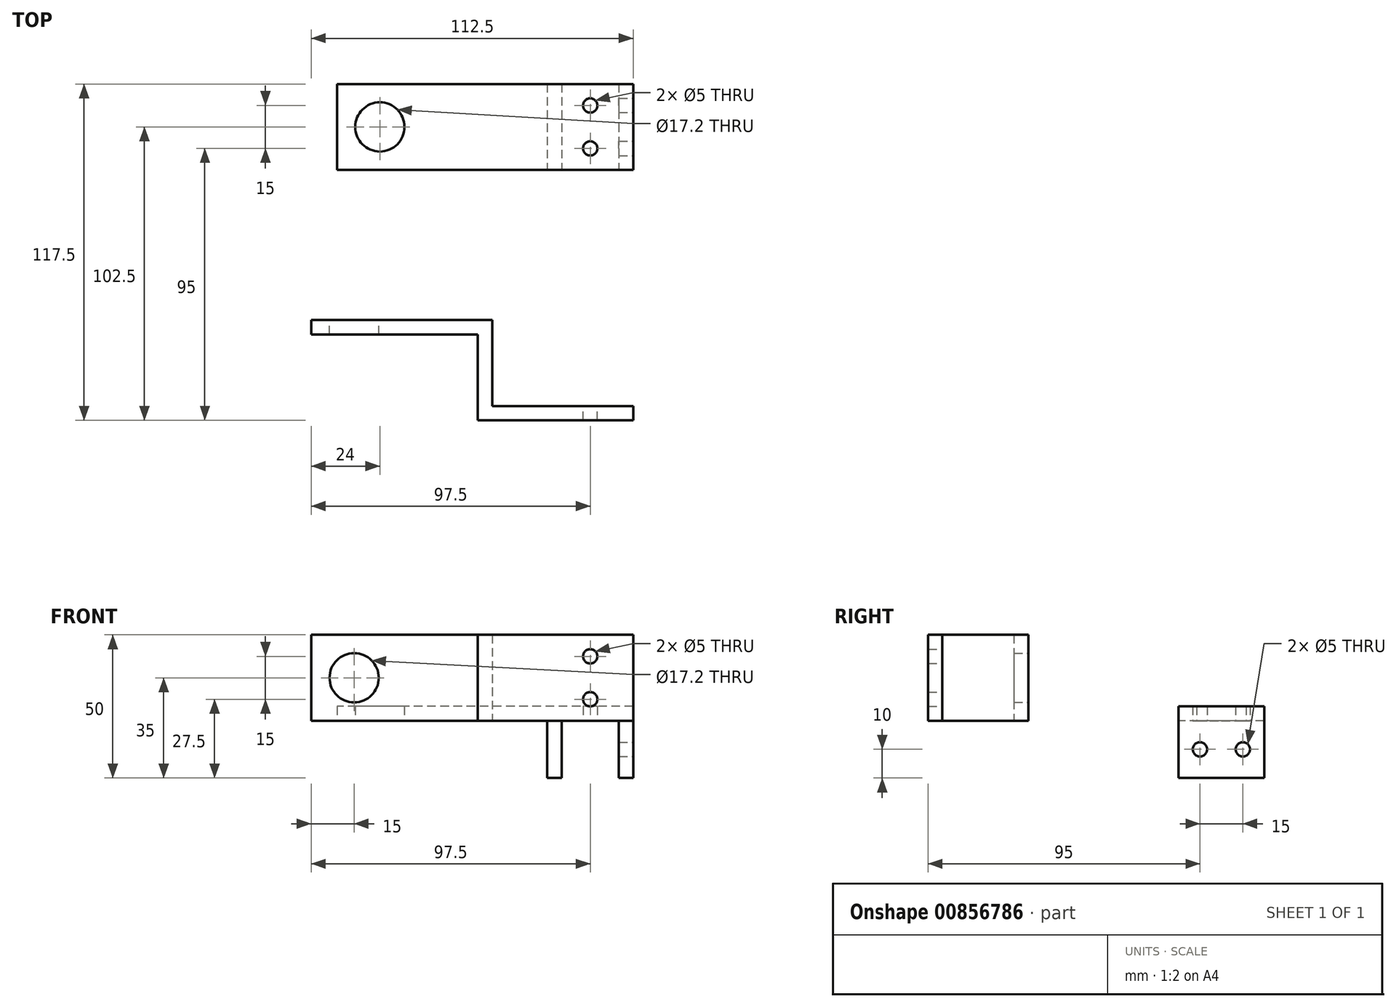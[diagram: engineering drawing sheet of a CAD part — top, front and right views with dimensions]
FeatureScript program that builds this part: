
annotation { "Feature Type Name" : "Feature", "Feature Type Description" : "" }
export const myFeature = defineFeature(function(context is Context, id is Id, definition is map)
    precondition{}
    {
        {
            var Q0;
            Q0=qCreatedBy(makeId("Top.planeOp"),FACE);
            var sketch = newSketch(context, id + "F0", { "sketchPlane" : qUnion([Q0])});
            skLineSegment(sketch, "E0.bottom", {"start": v(51.75, -15) * mm, "end": v(-51.75, -15) * mm});
            skLineSegment(sketch, "E0.top", {"start": v(51.75, 15) * mm, "end": v(-51.75, 15) * mm});
            skLineSegment(sketch, "E0.left", {"start": v(51.75, -15) * mm, "end": v(51.75, 15) * mm});
            skLineSegment(sketch, "E0.right", {"start": v(-51.75, -15) * mm, "end": v(-51.75, 15) * mm});
            skPoint(sketch, "E0.middle", {"position": v(0, 0) * mm});
            skLineSegment(sketch, "E1", {"start": v(46.75, 15) * mm, "end": v(46.75, -15) * mm});
            skCircle(sketch, "E2", {"center": v(-36.75, 0) * mm, "radius": 8.6 * mm});
            skLineSegment(sketch, "E3", {"start": v(26.75, 15) * mm, "end": v(26.75, -15) * mm});
            skLineSegment(sketch, "E4", {"start": v(21.75, 15) * mm, "end": v(21.75, -15) * mm});
            skCircle(sketch, "E5", {"center": v(36.75, 7.5) * mm, "radius": 2.5 * mm});
            skCircle(sketch, "E6", {"center": v(36.75, -7.5) * mm, "radius": 2.5 * mm});
            skLineSegment(sketch, "E7.bottom", {"start": v(51.75, -97.5) * mm, "end": v(-51.75, -97.5) * mm});
            skLineSegment(sketch, "E7.top", {"start": v(51.75, -102.5) * mm, "end": v(-51.75, -102.5) * mm});
            skLineSegment(sketch, "E7.left", {"start": v(51.75, -97.5) * mm, "end": v(51.75, -102.5) * mm});
            skLineSegment(sketch, "E7.right", {"start": v(-51.75, -97.5) * mm, "end": v(-51.75, -102.5) * mm});
            skPoint(sketch, "E7.middle", {"position": v(0, -100) * mm});
            skPoint(sketch, "E7.middle.positionSnap0", {"position": v(0, -15) * mm});
            skPoint(sketch, "E7.centerSnap0", {"position": v(0, -15) * mm});
            skLineSegment(sketch, "E8.bottom", {"start": v(51.75, -102.5) * mm, "end": v(46.75, -102.5) * mm});
            skLineSegment(sketch, "E8.top", {"start": v(51.75, -127.5) * mm, "end": v(46.75, -127.5) * mm});
            skLineSegment(sketch, "E8.left", {"start": v(51.75, -102.5) * mm, "end": v(51.75, -127.5) * mm});
            skLineSegment(sketch, "E8.right", {"start": v(46.75, -102.5) * mm, "end": v(46.75, -127.5) * mm});
            skLineSegment(sketch, "E9.bottom", {"start": v(21.75, -102.5) * mm, "end": v(26.75, -102.5) * mm});
            skLineSegment(sketch, "E9.top", {"start": v(21.75, -127.5) * mm, "end": v(26.75, -127.5) * mm});
            skLineSegment(sketch, "E9.left", {"start": v(21.75, -102.5) * mm, "end": v(21.75, -127.5) * mm});
            skLineSegment(sketch, "E9.right", {"start": v(26.75, -102.5) * mm, "end": v(26.75, -127.5) * mm});
            skLineSegment(sketch, "E10", {"start": v(2.5, -97.5) * mm, "end": v(2.5, -67.5) * mm});
            skLineSegment(sketch, "E11", {"start": v(2.5, -67.5) * mm, "end": v(-51.75, -67.5) * mm});
            skLineSegment(sketch, "E12", {"start": v(-51.75, -67.5) * mm, "end": v(-51.75, -72.5) * mm});
            skLineSegment(sketch, "E13", {"start": v(-51.75, -72.5) * mm, "end": v(-2.5, -72.5) * mm});
            skLineSegment(sketch, "E14", {"start": v(-2.5, -72.5) * mm, "end": v(-2.5, -97.5) * mm});
            skLineSegment(sketch, "E15", {"start": v(-2.5, -97.5) * mm, "end": v(-2.5, -102.5) * mm});
            skLineSegment(sketch, "E16", {"start": v(-51.75, -67.5) * mm, "end": v(-60.75, -67.5) * mm});
            skLineSegment(sketch, "E17", {"start": v(-60.75, -67.5) * mm, "end": v(-60.75, -72.5) * mm});
            skLineSegment(sketch, "E18", {"start": v(-60.75, -72.5) * mm, "end": v(-51.75, -72.5) * mm});
            skSolve(sketch);
        }
        {
            var Q0;
            {var subQ0=sQuery(id+"F0.wireOp",EDGE,"E0.left");Q0=makeQuery(id+"F0.imprint","IMPRINT",FACE,{"disambiguationData":[TD([[makeQuery(id+"F0.imprint","IMPRINT",EDGE,{"derivedFrom":subQ0}),1.0]])]});}
            var Q1;
            {var subQ0=sQuery(id+"F0.wireOp",EDGE,"E10");Q1=makeQuery(id+"F0.imprint","IMPRINT",FACE,{"disambiguationData":[TD([[makeQuery(id+"F0.imprint","IMPRINT",EDGE,{"derivedFrom":subQ0}),1.0]])]});}
            var Q2;
            Q2=makeQuery(id+"F0.imprint","IMPRINT",FACE,{"disambiguationData":[TD([[makeQuery(id+"F0.imprint","IMPRINT",EDGE,{"derivedFrom":sQuery(id+"F0.wireOp",EDGE,"E8.bottom")}),1.0]])]});
            var Q3;
            Q3=makeQuery(id+"F0.imprint","IMPRINT",FACE,{"disambiguationData":[TD([[makeQuery(id+"F0.imprint","IMPRINT",EDGE,{"derivedFrom":sQuery(id+"F0.wireOp",EDGE,"E9.bottom")}),-1.0]])]});
            var Q4;
            {var subQ0=sQuery(id+"F0.wireOp",EDGE,"E3");Q4=makeQuery(id+"F0.imprint","IMPRINT",FACE,{"disambiguationData":[TD([[makeQuery(id+"F0.imprint","IMPRINT",EDGE,{"derivedFrom":subQ0}),-1.0]])]});}
            var Q5;
            {var subQ0=sQuery(id+"F0.wireOp",EDGE,"E0.right");Q5=makeQuery(id+"F0.imprint","IMPRINT",FACE,{"disambiguationData":[TD([[makeQuery(id+"F0.imprint","IMPRINT",EDGE,{"derivedFrom":subQ0}),-1.0]])]});}
            var Q6;
            {var subQ1=sQuery(id+"F0.wireOp",EDGE,"E1");Q6=makeQuery(id+"F0.imprint","IMPRINT",FACE,{"disambiguationData":[TD([[makeQuery(id+"F0.imprint","IMPRINT",EDGE,{"derivedFrom":subQ1}),-1.0]])]});}
            var Q7;
            {var subQ6=sQuery(id+"F0.wireOp",EDGE,"E7.left");Q7=makeQuery(id+"F0.imprint","IMPRINT",FACE,{"disambiguationData":[TD([[makeQuery(id+"F0.imprint","IMPRINT",EDGE,{"derivedFrom":subQ6}),-1.0]])]});}
            extrude(context, id + "F1", {"entities" : qUnion([Q0, Q1, Q2, Q3, Q4, Q5, Q6, Q7]), "depth" : 5 * mm, "offsetDistance" : 25 * mm});
        }
        {
            var Q0;
            {var subQ0=sQuery(id+"F0.wireOp",EDGE,"E3");Q0=makeQuery(id+"F0.imprint","IMPRINT",FACE,{"disambiguationData":[TD([[makeQuery(id+"F0.imprint","IMPRINT",EDGE,{"derivedFrom":subQ0}),-1.0]])]});}
            var Q1;
            {var subQ0=sQuery(id+"F0.wireOp",EDGE,"E0.left");Q1=makeQuery(id+"F0.imprint","IMPRINT",FACE,{"disambiguationData":[TD([[makeQuery(id+"F0.imprint","IMPRINT",EDGE,{"derivedFrom":subQ0}),1.0]])]});}
            extrude(context, id + "F2", {"entities" : qUnion([Q0, Q1]), "operationType" : NewBodyOperationType.ADD, "oppositeDirection" : true, "depth" : 20 * mm, "offsetDistance" : 25 * mm});
        }
        {
            var Q0;
            {var subQ0=sQuery(id+"F0.wireOp",EDGE,"E0.left");Q0=makeQuery(id+"F2.boolean.opBoolean","MERGE",FACE,{"derivedFrom":[makeQuery(id+"F1.opExtrude","SWEPT_FACE",FACE,{"disambiguationData":[OSD([subQ0])]}),makeQuery(id+"F2.opExtrude","SWEPT_FACE",FACE,{"disambiguationData":[OSD([subQ0])]})]});}
            var sketch = newSketch(context, id + "F3", { "sketchPlane" : qUnion([Q0])});
            skCircle(sketch, "E19", {"center": v(-7.5, -10) * mm, "radius": 2.5 * mm});
            skCircle(sketch, "E20.MirrorC", {"center": v(7.5, -10) * mm, "radius": 2.5 * mm});
            skSolve(sketch);
        }
        {
            var Q0;
            Q0 = qSketchRegion(id + "F3", true);
            extrude(context, id + "F4", {"entities" : qUnion([Q0]), "operationType" : NewBodyOperationType.REMOVE, "oppositeDirection" : true, "depth" : 10 * mm, "offsetDistance" : 25 * mm});
        }
        {
            var Q0;
            {var subQ0=sQuery(id+"F0.wireOp",EDGE,"E10");Q0=makeQuery(id+"F0.imprint","IMPRINT",FACE,{"disambiguationData":[TD([[makeQuery(id+"F0.imprint","IMPRINT",EDGE,{"derivedFrom":subQ0}),1.0]])]});}
            var Q1;
            {var subQ6=sQuery(id+"F0.wireOp",EDGE,"E7.left");Q1=makeQuery(id+"F0.imprint","IMPRINT",FACE,{"disambiguationData":[TD([[makeQuery(id+"F0.imprint","IMPRINT",EDGE,{"derivedFrom":subQ6}),-1.0]])]});}
            var Q2;
            Q2=makeQuery(id+"F0.imprint","IMPRINT",FACE,{"disambiguationData":[TD([[makeQuery(id+"F0.imprint","IMPRINT",EDGE,{"derivedFrom":sQuery(id+"F0.wireOp",EDGE,"E9.bottom")}),-1.0]])]});
            var Q3;
            Q3=makeQuery(id+"F0.imprint","IMPRINT",FACE,{"disambiguationData":[TD([[makeQuery(id+"F0.imprint","IMPRINT",EDGE,{"derivedFrom":sQuery(id+"F0.wireOp",EDGE,"E8.bottom")}),1.0]])]});
            var Q4;
            Q4=makeQuery(id+"F0.imprint","IMPRINT",FACE,{"disambiguationData":[TD([[makeQuery(id+"F0.imprint","IMPRINT",EDGE,{"derivedFrom":sQuery(id+"F0.wireOp",EDGE,"E12")}),-1.0]])]});
            extrude(context, id + "F5", {"entities" : qUnion([Q0, Q1, Q2, Q3, Q4]), "operationType" : NewBodyOperationType.ADD, "flatOperationType" : FlatOperationType.REMOVE, "depth" : 30 * mm, "offsetDistance" : 25 * mm, "domain" : OperationDomain.MODEL});
        }
        {
            var Q0;
            {var subQ0=sQuery(id+"F0.wireOp",EDGE,"E11");Q0=makeQuery(id+"F5.boolean.opBoolean","MERGE",FACE,{"derivedFrom":[makeQuery(id+"F1.opExtrude","SWEPT_FACE",FACE,{"disambiguationData":[OSD([subQ0])]}),makeQuery(id+"F5.opExtrude","SWEPT_FACE",FACE,{"disambiguationData":[OSD([subQ0])]})]});}
            var sketch = newSketch(context, id + "F6", { "sketchPlane" : qUnion([Q0])});
            skCircle(sketch, "E21", {"center": v(45.75, 15) * mm, "radius": 8.6 * mm});
            skPoint(sketch, "E21.centerSnap0", {"position": v(-2.5, 15) * mm});
            skSolve(sketch);
        }
        {
            var Q0;
            Q0 = qSketchRegion(id + "F6", true);
            extrude(context, id + "F7", {"entities" : qUnion([Q0]), "operationType" : NewBodyOperationType.REMOVE, "oppositeDirection" : true, "depth" : 5 * mm, "offsetDistance" : 25 * mm});
        }
        {
            var Q0;
            {var subQ0=sQuery(id+"F0.wireOp",EDGE,"E7.bottom");Q0=makeQuery(id+"F5.boolean.opBoolean","MERGE",FACE,{"derivedFrom":[makeQuery(id+"F1.opExtrude","SWEPT_FACE",FACE,{"disambiguationData":[OSD([subQ0])]}),makeQuery(id+"F5.opExtrude","SWEPT_FACE",FACE,{"disambiguationData":[OSD([subQ0])]})]});}
            var sketch = newSketch(context, id + "F8", { "sketchPlane" : qUnion([Q0])});
            skCircle(sketch, "E22", {"center": v(-36.75, 7.5) * mm, "radius": 2.5 * mm});
            skCircle(sketch, "E23", {"center": v(-36.75, 22.5) * mm, "radius": 2.5 * mm});
            skSolve(sketch);
        }
        {
            var Q0;
            Q0 = qSketchRegion(id + "F8", true);
            extrude(context, id + "F9", {"entities" : qUnion([Q0]), "operationType" : NewBodyOperationType.REMOVE, "oppositeDirection" : true, "depth" : 5 * mm, "offsetDistance" : 25 * mm});
        }
        {
            var Q0;
            {var subQ0=sQuery(id+"F0.wireOp",EDGE,"E8.left");var subQ1=sQuery(id+"F0.wireOp",EDGE,"E7.left");Q0=makeQuery(id+"F5.boolean.opBoolean","MERGE",FACE,{"derivedFrom":[makeQuery(id+"F1.opExtrude","SWEPT_FACE",FACE,{"disambiguationData":[OSD([subQ1,subQ0])]}),makeQuery(id+"F5.opExtrude","SWEPT_FACE",FACE,{"disambiguationData":[OSD([subQ1,subQ0])]})]});}
            var sketch = newSketch(context, id + "F10", { "sketchPlane" : qUnion([Q0])});
            skCircle(sketch, "E24", {"center": v(-112.5, 22.5) * mm, "radius": 2.5 * mm});
            skCircle(sketch, "E25", {"center": v(-112.5, 7.5) * mm, "radius": 2.5 * mm});
            skSolve(sketch);
        }
        {
            var Q0;
            Q0 = qSketchRegion(id + "F10", true);
            extrude(context, id + "F11", {"entities" : qUnion([Q0]), "operationType" : NewBodyOperationType.REMOVE, "oppositeDirection" : true, "depth" : 5 * mm, "offsetDistance" : 25 * mm});
        }
    });
